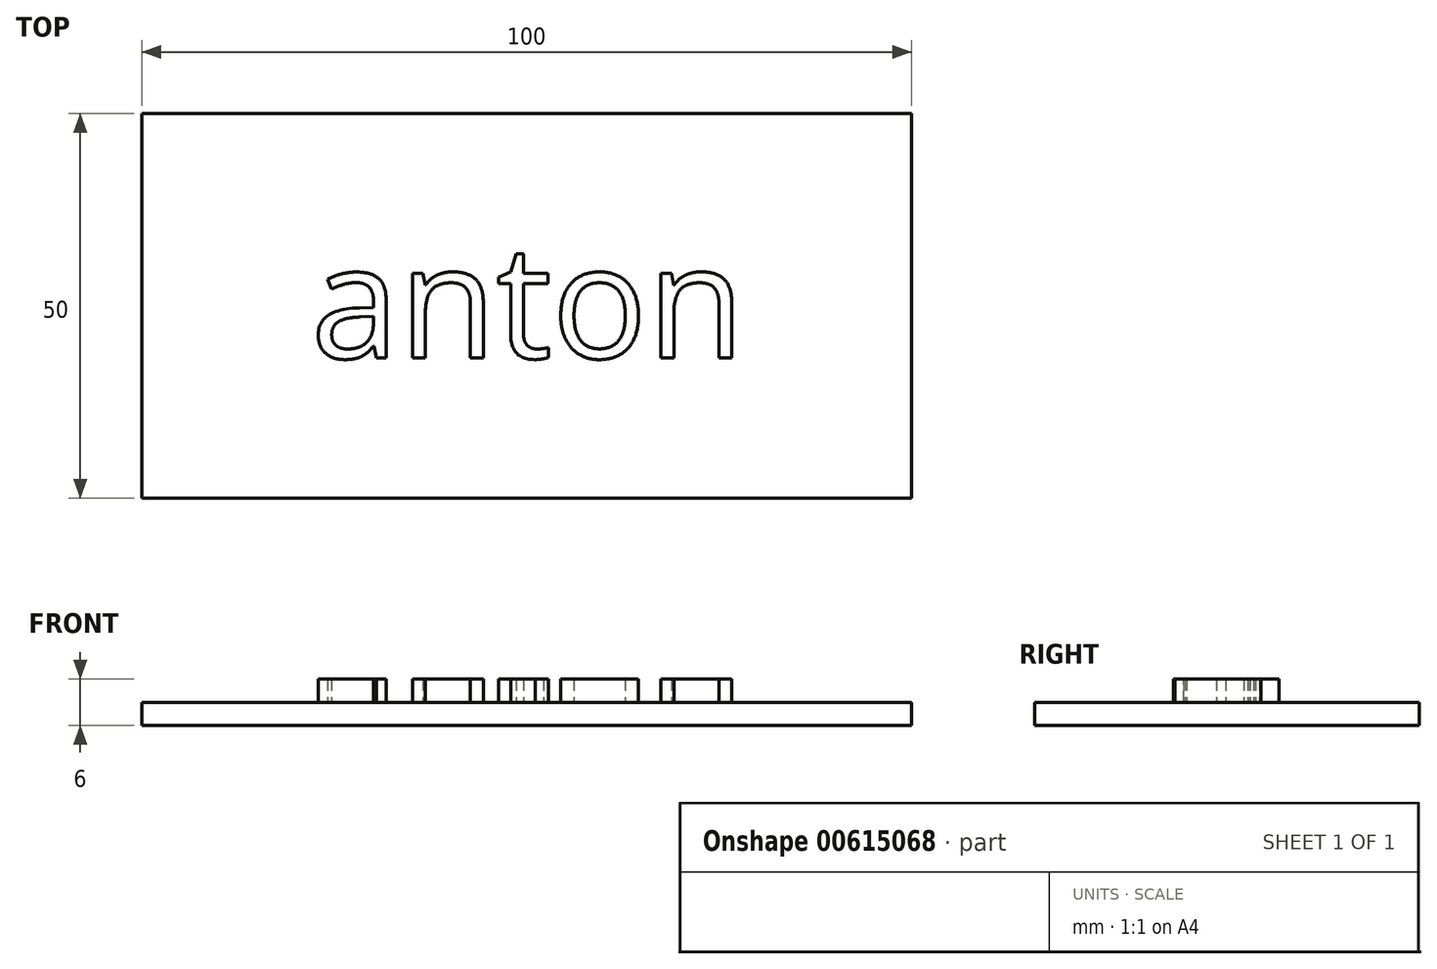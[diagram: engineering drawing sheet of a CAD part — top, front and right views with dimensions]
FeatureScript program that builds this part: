
annotation { "Feature Type Name" : "Feature", "Feature Type Description" : "" }
export const myFeature = defineFeature(function(context is Context, id is Id, definition is map)
    precondition{}
    {
        {
            var Q0;
            Q0=qCreatedBy(makeId("Top.planeOp"),FACE);
            var sketch = newSketch(context, id + "F0", { "sketchPlane" : qUnion([Q0])});
            skLineSegment(sketch, "E0.bottom", {"start": v(0, 0) * mm, "end": v(100, 0) * mm});
            skLineSegment(sketch, "E0.top", {"start": v(0, 50) * mm, "end": v(100, 50) * mm});
            skLineSegment(sketch, "E0.left", {"start": v(0, 0) * mm, "end": v(0, 50) * mm});
            skLineSegment(sketch, "E0.right", {"start": v(100, 0) * mm, "end": v(100, 50) * mm});
            skLineSegment(sketch, "E1.bottom", {"start": v(100, 50) * mm, "end": v(96.75, 50) * mm});
            skLineSegment(sketch, "E1.top", {"start": v(100, 50) * mm, "end": v(96.75, 50) * mm});
            skLineSegment(sketch, "E1.left", {"start": v(100, 50) * mm, "end": v(100, 50) * mm});
            skLineSegment(sketch, "E1.right", {"start": v(96.75, 50) * mm, "end": v(96.75, 50) * mm});
            skSolve(sketch);
        }
        {
            var Q0;
            Q0=makeQuery(id+"F0.imprint","IMPRINT",FACE,{"disambiguationData":[TD([[makeQuery(id+"F0.imprint","IMPRINT",EDGE,{"derivedFrom":sQuery(id+"F0.wireOp",EDGE,"E0.bottom")}),1.0]])]});
            extrude(context, id + "F1", {"entities" : qUnion([Q0]), "depth" : 3 * mm, "offsetDistance" : 25 * mm});
        }
        {
            var Q0;
            Q0=makeQuery(id+"F1.opExtrude","CAP_FACE",FACE,{"disambiguationData":[OSD([sQuery(id+"F0.wireOp",EDGE,"E0.bottom"),sQuery(id+"F0.wireOp",EDGE,"E0.top"),sQuery(id+"F0.wireOp",EDGE,"E0.left"),sQuery(id+"F0.wireOp",EDGE,"E0.right"),sQuery(id+"F0.wireOp",EDGE,"E1.top")])],"isStart":false});
            var sketch = newSketch(context, id + "F2", { "sketchPlane" : qUnion([Q0])});
            skText(sketch, "E2", { "text": "anton", "fontName": "OpenSans-Regular.ttf"});
            const initialGuessF2  = {"E2": [0.02197, 0.01822, 1, 0, 0.0148]};
            skSetInitialGuess(sketch, initialGuessF2);
            skSolve(sketch);
        }
        {
            var Q0;
            Q0 = qSketchRegion(id + "F2", true);
            extrude(context, id + "F3", {"entities" : qUnion([Q0]), "operationType" : NewBodyOperationType.ADD, "depth" : 3 * mm, "offsetDistance" : 25 * mm});
        }
    });
